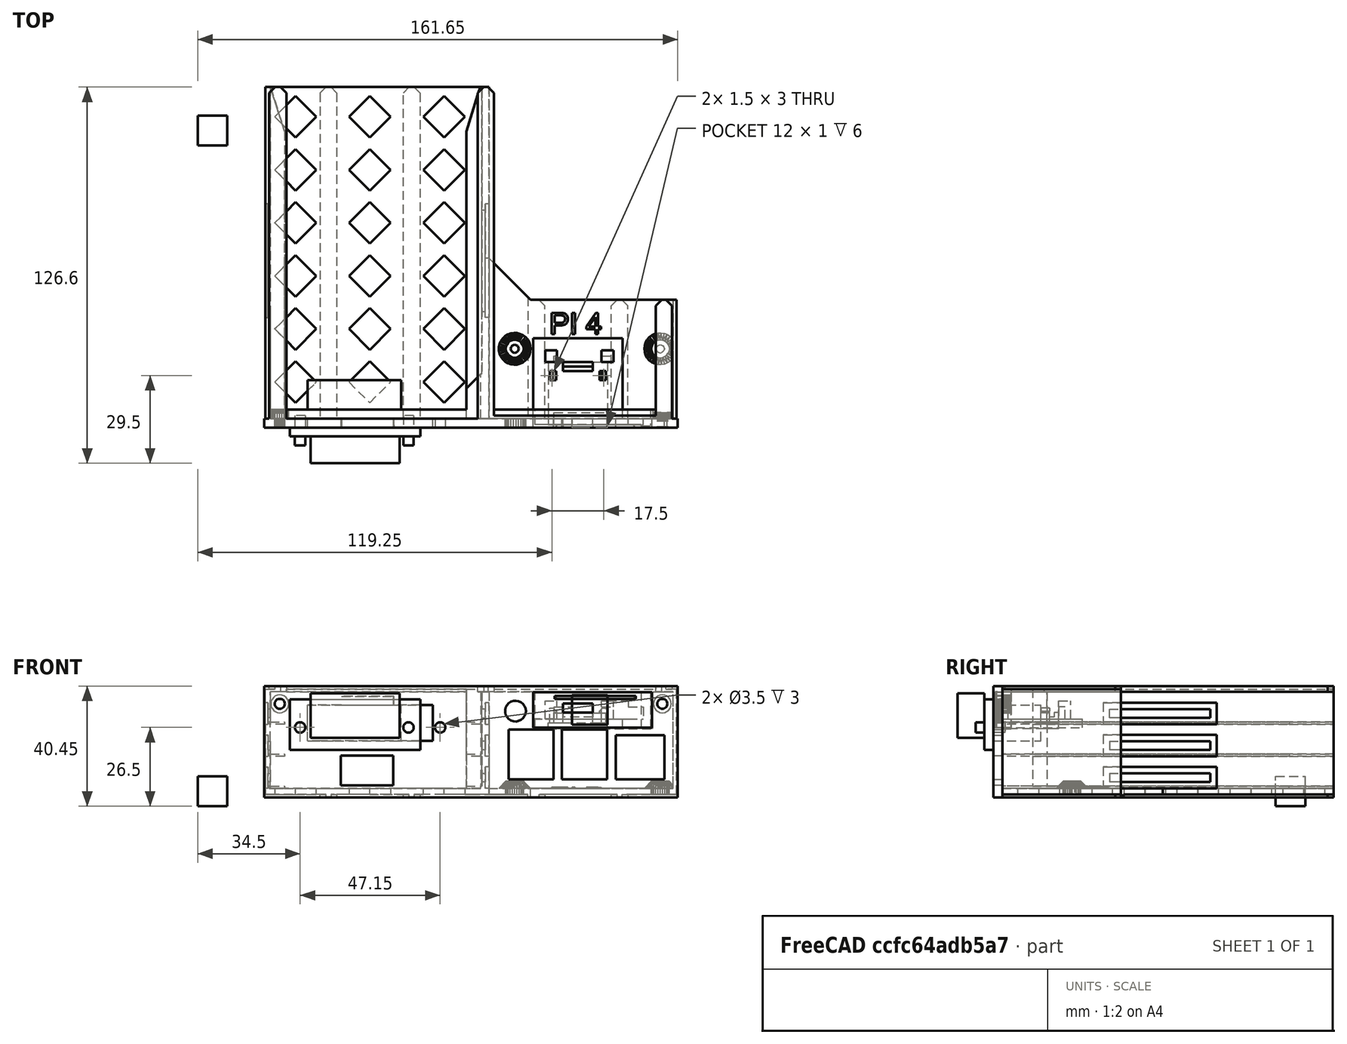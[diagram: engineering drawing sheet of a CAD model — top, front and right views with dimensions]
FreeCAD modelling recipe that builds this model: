
FCSTD DOCUMENT  (FreeCAD 0.19R24291 (Git))
Label: trpi4-1
License: All rights reserved
LicenseURL: http://en.wikipedia.org/wiki/All_rights_reserved
objects: Part::Box×23, Part::MultiFuse×10, Part::Cut×7, Part::Cylinder×4, Part::Feature×2, Part::Chamfer×1
note: 47 computed .brp shape members not serialized (recipe doc carries the construction recipe); baked Part::Feature solids carry a one-line shape summary decoded from their .brp

FEATURE [Part::Box] Box  label="Cube"
  AttacherType = Attacher::AttachEngine3D
  Height = 10
  Length = 18
  Placement = pos=(48,-95,27) rot=(0,0,1;0rad)
  Width = 3
FEATURE [Part::Feature] tpi4001
  shape: bbox 139.2 x 114.6 x 37.45 mm, 2746 faces, 0 solids (baked)
FEATURE [Part::Feature] tpi4001_solid  label="tpi4001 (Solid)"
  shape: bbox 139.2 x 114.6 x 37.45 mm, 2746 faces (baked)
FEATURE [Part::MultiFuse] Fusion
  Shapes = -> [tpi4001_solid,Box]
FEATURE [Part::Box] Box006  label="Cube006"
  AttacherType = Attacher::AttachEngine3D
  Height = 5
  Length = 19
  Placement = pos=(7,1,0) rot=(0,0,1;0rad)
  Width = 4
FEATURE [Part::Box] Box003  label="Cube003"
  AttacherType = Attacher::AttachEngine3D
  Height = 10
  Length = 12
  Placement = pos=(13,-4,1) rot=(0,0,1;0rad)
  Width = 7
FEATURE [Part::Box] Box004  label="Cube004"
  AttacherType = Attacher::AttachEngine3D
  Height = 6
  Length = 4
  Placement = pos=(23,22,3) rot=(0,0,1;0rad)
  Width = 4
FEATURE [Part::Box] Box005  label="Cube005"
  AttacherType = Attacher::AttachEngine3D
  Height = 6
  Length = 4
  Placement = pos=(4,22,3) rot=(0,0,1;0rad)
  Width = 4
FEATURE [Part::Box] Box001  label="Cube001"
  AttacherType = Attacher::AttachEngine3D
  Height = 12
  Length = 40
  Width = 3
FEATURE [Part::Box] Box002  label="Cube002"
  AttacherType = Attacher::AttachEngine3D
  Height = 4
  Length = 30.1
  Placement = pos=(7,1,3) rot=(0,0,1;0rad)
  Width = 23.1
FEATURE [Part::Box] Box007  label="Cube007"
  AttacherType = Attacher::AttachEngine3D
  Height = 6
  Length = 7
  Placement = pos=(25,1,3) rot=(0,0,1;0rad)
  Width = 4
FEATURE [Part::Box] Box008  label="Cube008"
  AttacherType = Attacher::AttachEngine3D
  Height = 3
  Length = 30
  Width = 30
FEATURE [Part::MultiFuse] Fusion001
  Shapes = -> [Box008,Box001,Box004,Box005]
FEATURE [Part::Cut] Cut
  Base = -> Fusion001
  Tool = -> Box003
FEATURE [Part::Cut] Cut001
  Base = -> Cut
  Tool = -> Box002
FEATURE [Part::MultiFuse] Fusion002
  Shapes = -> [Box006,Cut001]
FEATURE [Part::Cut] Cut002  label="ttl-usb-ver1"
  Base = -> Fusion002
  Placement = pos=(113,-95,26.4) rot=(0,0,1;0rad)
  Tool = -> Box007
FEATURE [Part::Box] Box009  label="Cube009"
  AttacherType = Attacher::AttachEngine3D
  Height = 17
  Length = 44
  Placement = pos=(36,-98,19) rot=(0,0,1;0rad)
  Width = 3
FEATURE [Part::Box] Box010  label="Cube010"
  AttacherType = Attacher::AttachEngine3D
  Height = 15
  Length = 30
  Placement = pos=(43,-107,23) rot=(0,0,1;0rad)
  Width = 9
FEATURE [Part::Cylinder] Cylinder
  Angle = 360
  AttacherType = Attacher::AttachEngine3D
  Height = 10
  Placement = pos=(40,-91,26.5) rot=(1,0,0;1.5708rad)
  Radius = 1.75
FEATURE [Part::Cylinder] Cylinder001
  Angle = 360
  AttacherType = Attacher::AttachEngine3D
  Height = 10
  Placement = pos=(76.5,-91,26.5) rot=(1,0,0;1.5708rad)
  Radius = 1.75
FEATURE [Part::Box] Box011  label="Cube011"
  AttacherType = Attacher::AttachEngine3D
  Height = 12
  Length = 31.5
  Placement = pos=(42,-95,22) rot=(0,0,1;0rad)
  Width = 16
FEATURE [Part::MultiFuse] Fusion003
  Placement = pos=(-0.5,0,0) rot=(0,0,1;0rad)
  Shapes = -> [Cylinder001,Cylinder]
FEATURE [Part::MultiFuse] Fusion004  label="4P"
  Placement = pos=(-5,0,0) rot=(0,0,1;0rad)
  Shapes = -> [Box009,Box010,Box011,Fusion003]
FEATURE [Part::Box] Box013  label="Cube013"
  AttacherType = Attacher::AttachEngine3D
  Height = 12
  Length = 42.2
  Placement = pos=(5.97,-10,0.8) rot=(0,0,1;0rad)
  Width = 9
FEATURE [Part::Cylinder] Cylinder002
  Angle = 360
  AttacherType = Attacher::AttachEngine3D
  Height = 10
  Placement = pos=(47.15,0,0) rot=(1,0,0;1.5708rad)
  Radius = 1.75
FEATURE [Part::Cylinder] Cylinder003
  Angle = 360
  AttacherType = Attacher::AttachEngine3D
  Height = 10
  Placement = pos=(0,0,0) rot=(1,0,0;1.5708rad)
  Radius = 1.75
FEATURE [Part::MultiFuse] Fusion005
  Placement = pos=(3.5,0,5.3) rot=(0,0,1;0rad)
  Shapes = -> [Cylinder003,Cylinder002]
FEATURE [Part::MultiFuse] Fusion006  label="6P"
  Placement = pos=(31,-91,21.2) rot=(0,0,1;0rad)
  Shapes = -> [Box013,Fusion005]
FEATURE [Part::Cut] Cut003  label="rpi4-tray"
  Base = -> Fusion
  Tool = -> Fusion006
FEATURE [Part::Box] Box014  label="Cube014"
  AttacherType = Attacher::AttachEngine3D
  Height = 5.5
  Length = 3
  Placement = pos=(-3,3,-3.5) rot=(0,0,1;0rad)
  Width = 10
  expr: .Placement.Base.z = -3.5
FEATURE [Part::Box] Box015  label="Cube015"
  AttacherType = Attacher::AttachEngine3D
  Height = 2
  Length = 21
  Placement = pos=(-3,-2,-3.5) rot=(0,0,1;0rad)
  Width = 20
FEATURE [Part::Box] Box016  label="Cube016"
  AttacherType = Attacher::AttachEngine3D
  Height = 5.5
  Length = 3
  Placement = pos=(16,3,-3.5) rot=(0,0,1;0rad)
  Width = 10
  expr: .Placement.Base.z = -3.5
FEATURE [Part::Box] Box017  label="Cube017"
  AttacherType = Attacher::AttachEngine3D
  Height = 3
  Length = 2
  Placement = pos=(18,3,2) rot=(0,0,1;0rad)
  Width = 10
FEATURE [Part::Box] Box018  label="Cube018"
  AttacherType = Attacher::AttachEngine3D
  Height = 7
  Length = 3
  Placement = pos=(0,0,-5) rot=(0,0,1;0rad)
  Width = 16
FEATURE [Part::Box] Box019  label="ttl-usb-board"
  AttacherType = Attacher::AttachEngine3D
  Height = 1.6
  Length = 19.5
  Placement = pos=(-1.5,0,0.4) rot=(0,0,1;0rad)
  Width = 16
FEATURE [Part::Box] Box020  label="Cube020"
  AttacherType = Attacher::AttachEngine3D
  Height = 10
  Length = 3
  Placement = pos=(0,0.75,-3) rot=(0,0,1;0rad)
  Width = 14.5
FEATURE [Part::Box] Box021  label="Cube021"
  AttacherType = Attacher::AttachEngine3D
  Height = 10
  Length = 1
  Placement = pos=(18,-2,-3.5) rot=(0,0,1;0rad)
  Width = 30
FEATURE [Part::MultiFuse] Fusion008
  Shapes = -> [Box018,Box020]
FEATURE [Part::Cut] Cut006
  Base = -> Box021
  Tool = -> Box017
FEATURE [Part::Box] Box022  label="Cube022"
  AttacherType = Attacher::AttachEngine3D
  Height = 7
  Length = 3
  Placement = pos=(0,-1.5,-3.5) rot=(0,0,1;0rad)
  Width = 19
FEATURE [Part::Cut] Cut004
  Base = -> Box022
  Tool = -> Fusion008
FEATURE [Part::Chamfer] Chamfer
  Base = -> Cut004
  Edges = 2 edges r=1: [Edge7,Edge27]
FEATURE [Part::MultiFuse] Fusion007
  Shapes = -> [Box014,Box015,Chamfer,Cut006,Box016]
FEATURE [Part::Cut] Cut005  label="ttl-usb-ver2"
  Base = -> Fusion007
  Placement = pos=(120,-76,29.55) rot=(0,0,-1;1.5708rad)
  Tool = -> Box019
FEATURE [Part::MultiFuse] Fusion009  label="rpi4-tray-all"
  Shapes = -> [Cut005,Cut003]
FEATURE [Part::Box] Box023  label="Cube023"
  AttacherType = Attacher::AttachEngine3D
  Height = 10
  Length = 10
  Width = 10
